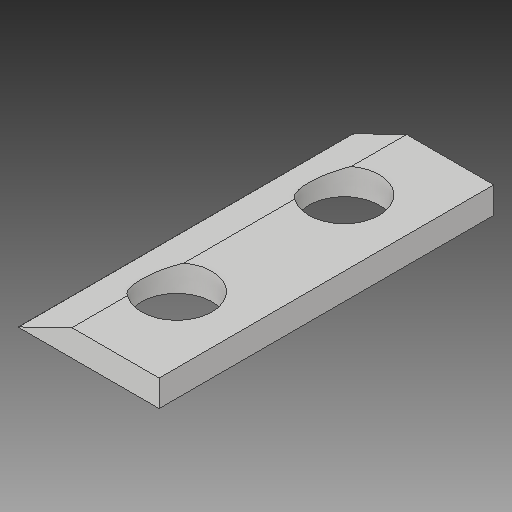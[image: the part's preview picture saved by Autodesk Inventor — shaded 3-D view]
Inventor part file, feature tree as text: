
AUTODESK INVENTOR PART (.ipt)
format: ipt  version: 2017 (Build 210142000, 142)  size: 116,224 bytes
history: native  units: in
note: dims shown in document units (in); Inventor stores cm internally (conversion verified against a paired STEP export)
features: other x3, extrude x2, hole x2, sketch x2, reference x1
ambient origin geometry x8: Origin, YZ Plane, XZ Plane, XY Plane, X Axis, Y Axis, Z Axis, Center Point
bodies: Solid1 (feature_tree)
feature tree (10):
  extrude  "Extrusion1"  Depth=9.5in
  hole  "Hole1"  [1 undecoded]
  hole  "Hole2"  [1 undecoded]
  extrude  "Extrusion3"  [1 undecoded]
  sketch  "Sketch1"  dims[d0=4.0in d1=9.5in]
  sketch  "Sketch3"  dims[d2=0.75in d3=0.0in d4=2.125in d5=2.375in d6=2.0in d7=0.75in d8=0.375in d9=0.25in d10=0.5635in d11=1.0in d12=0.8108in d13=2.125in d14=2.375in d15=2.0in d16=0.75in d17=0.375in d18=0.25in d19=0.5635in d20=1.0in d21=0.8108in d25=9.5in d26=0.0in]
  reference  "Reference2"
  parser-record x1  (decoder bookkeeping rows leaked as tree rows — omitted from the tree; the rows remain in map.json)
  other  "Arcade.iam"
  other  "Marque:1"
note: 3 required parameter values undecoded (feature->parameter linkage not recoverable at this tier; creation-order binding heuristic only, values carry confidence <= 0.55)
note: 1 file-system path scrubbed to <path> (originals preserved in map.json)
